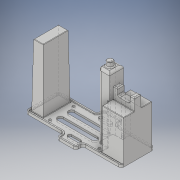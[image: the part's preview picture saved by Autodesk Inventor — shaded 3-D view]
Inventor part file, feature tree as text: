
AUTODESK INVENTOR PART (.ipt)
format: ipt  version: 2019.1 (Build 231200000, 200)  size: 484,352 bytes
history: native  units: in
note: dims shown in document units (in); Inventor stores cm internally (conversion verified against a paired STEP export)
features: extrude x9, fillet x9, sketch x8, draft x1, projected_geometry x1
ambient origin geometry x8: Origin, YZ Plane, XZ Plane, XY Plane, X Axis, Y Axis, Z Axis, Center Point
bodies: Solid1 (feature_tree)
feature tree (28):
  extrude  "Base"  Depth=2.7559in
  extrude  "Chassis"  Depth=0.9646in
  draft  "FaceDraft2"
  extrude  "Step"  Depth=1.7717in
  extrude  "RearWheels"  Depth=5.7874in
  extrude  "Edge"  Depth=1.7717in
  sketch  "Sketch9"  dims[d23=1.7717in d24=0.3642in]
  fillet  "Fillet1mm"  Radius=2.3622in
  fillet  "Fillet4mm"  Radius=3.4252in
  fillet  "Fillet3"  Radius=0.1969in
  extrude  "Pin"  Depth=1.0433in
  fillet  "Fillet4"  Radius=0.6102in
  extrude  "Extrusion7"  Depth=0.3642in
  extrude  "Extrusion8"  Depth=0.0787in TaperAngle=0.0deg
  extrude  "Extrusion10"  Depth=0.0354in
  fillet  "Fillet5"  Radius=0.1575in
  fillet  "Fillet6"  Radius=0.0787in
  fillet  "Fillet7"  Radius=0.0062in
  fillet  "Fillet10"  Radius=5.9055in
  fillet  "Fillet11"  Radius=0.2362in
  sketch  "Sketch2"  dims[d0=7.9921in d1=2.7559in]
  sketch  "Sketch3"  dims[d4=0.1575in d5=0.0in d6=0.9646in]
  sketch  "Sketch4"  dims[d7=2.2441in d8=1.7717in]
  sketch  "Sketch5"  dims[d9=2.3622in d10=5.7874in]
  projected_geometry  "Projected Loop2"
  sketch  "Sketch6"  dims[d12=5.2362in d13=0.0in d15=1.7717in d16=2.3622in d17=3.4252in d18=0.0in d19=0.1969in]
  sketch  "Sketch7"  dims[d20=0.9843in d21=1.0433in d22=0.6102in]
  sketch  "Sketch11"  dims[d25=0.5512in d26=0.0in d29=0.0787in d30=0.0in d31=0.0354in d32=0.1575in d33=0.0787in d37=0.0062in d38=5.9055in d40=0.2362in d41=0.4921in d42=1.7913in d43=0.8957in d44=1.4173in d45=5.8661in d46=0.0in d47=0.0394in d48=1.5748in d49=3.937in d50=0.1969in d51=0.1181in d52=0.1969in d56=2.3622in d60=0.9843in d62=0.4724in d63=0.3937in d64=0.0in d65=0.1969in d66=1.7717in d67=0.9843in d68=0.3937in d69=0.315in d70=5.4724in d71=0.9055in d72=0.0in d73=0.0787in d74=0.0787in d75=0.0197in d83=0.5906in d84=0.5906in d85=0.3937in d86=0.0in d87=0.1969in d88=0.0394in d89=0.1575in]
